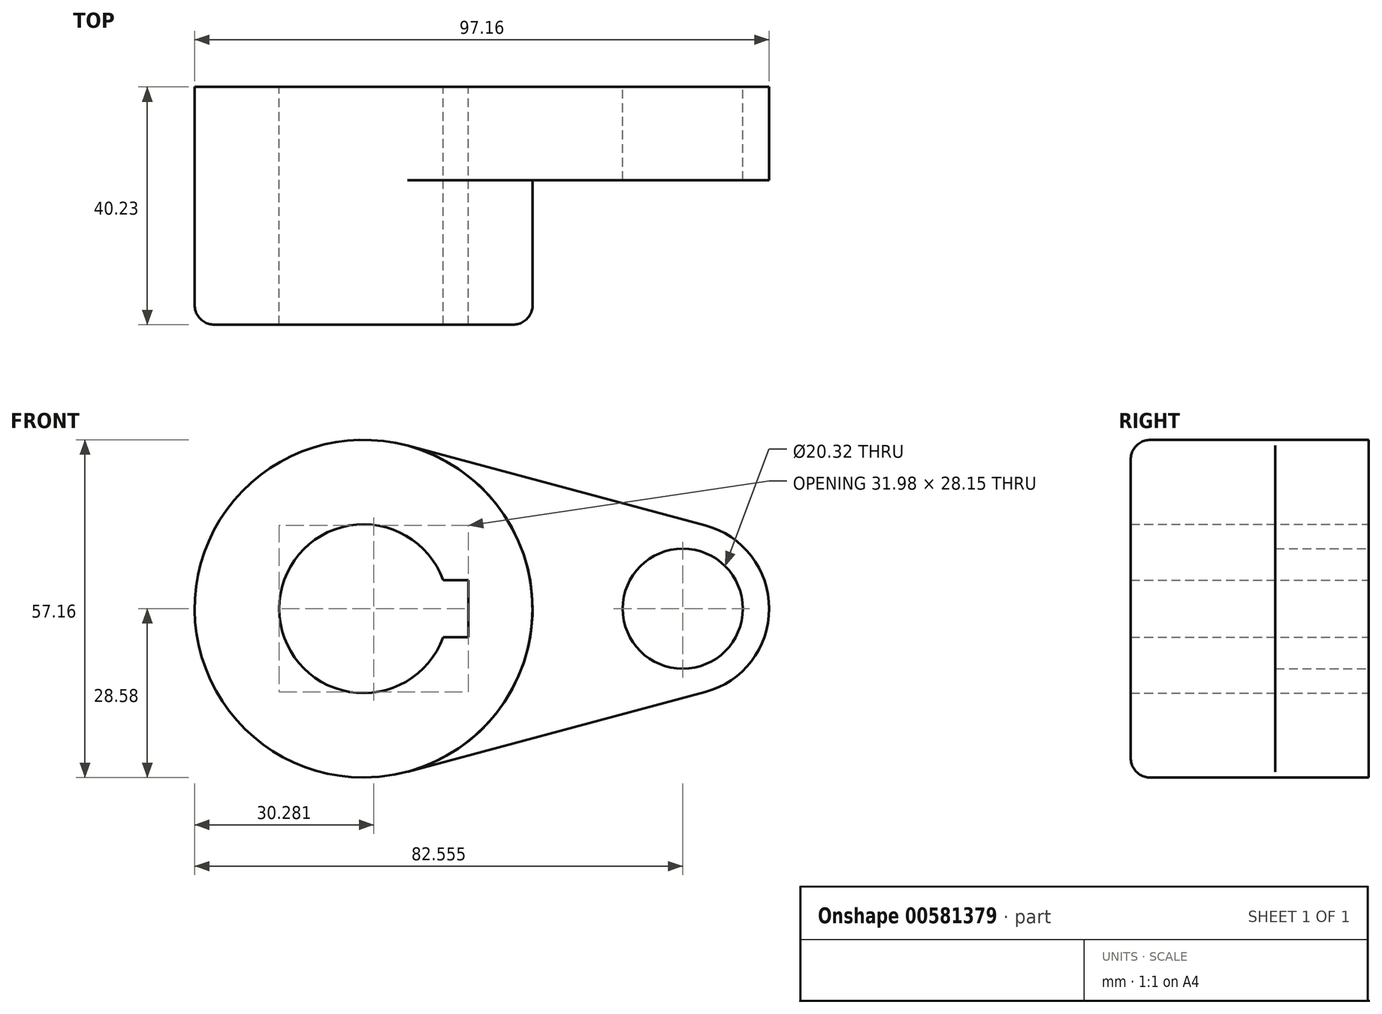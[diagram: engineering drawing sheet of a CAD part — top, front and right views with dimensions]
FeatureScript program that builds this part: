
annotation { "Feature Type Name" : "Feature", "Feature Type Description" : "" }
export const myFeature = defineFeature(function(context is Context, id is Id, definition is map)
    precondition{}
    {
        {
            var Q0;
            Q0=qCreatedBy(makeId("Front.planeOp"),FACE);
            var sketch = newSketch(context, id + "F0", { "sketchPlane" : qUnion([Q0])});
            skCircle(sketch, "E0", {"center": v(0, 0) * mm, "radius": 28.58 * mm});
            skCircle(sketch, "E1", {"center": v(0, 0) * mm, "radius": 14.29 * mm});
            skLineSegment(sketch, "E2", {"start": v(0, 0) * mm, "end": v(53.98, 0) * mm, "construction": true});
            skCircle(sketch, "E3", {"center": v(53.98, 0) * mm, "radius": 10.16 * mm});
            skCircle(sketch, "E4", {"center": v(53.98, 0) * mm, "radius": 14.6 * mm});
            skLineSegment(sketch, "E5", {"start": v(7.4, 27.6) * mm, "end": v(57.76, 14.1) * mm});
            skLineSegment(sketch, "E6", {"start": v(7.4, -27.6) * mm, "end": v(57.76, -14.1) * mm});
            skLineSegment(sketch, "E7", {"start": v(13.45, 4.83) * mm, "end": v(17.69, 4.83) * mm});
            skLineSegment(sketch, "E8", {"start": v(17.69, 4.83) * mm, "end": v(17.69, -4.83) * mm});
            skLineSegment(sketch, "E9", {"start": v(17.69, -4.83) * mm, "end": v(13.45, -4.83) * mm});
            skSolve(sketch);
        }
        {
            var Q0;
            {var subQ0=sQuery(id+"F0.wireOp",EDGE,"E7");Q0=makeQuery(id+"F0.imprint","IMPRINT",FACE,{"disambiguationData":[TD([[makeQuery(id+"F0.imprint","IMPRINT",EDGE,{"derivedFrom":subQ0}),1.0]])]});}
            extrude(context, id + "F1", {"entities" : qUnion([Q0]), "depth" : 40.23 * mm, "offsetDistance" : 25.4 * mm});
        }
        {
            var Q0;
            {var subQ0=sQuery(id+"F0.wireOp",EDGE,"E5");Q0=makeQuery(id+"F0.imprint","IMPRINT",FACE,{"disambiguationData":[TD([[makeQuery(id+"F0.imprint","IMPRINT",EDGE,{"derivedFrom":subQ0}),-1.0]])]});}
            var Q1;
            Q1=makeQuery(id+"F0.imprint","IMPRINT",FACE,{"disambiguationData":[TD([[makeQuery(id+"F0.imprint","IMPRINT",EDGE,{"derivedFrom":sQuery(id+"F0.wireOp",EDGE,"E3")}),-1.0]])]});
            extrude(context, id + "F2", {"entities" : qUnion([Q0, Q1]), "operationType" : NewBodyOperationType.ADD, "depth" : 15.77 * mm, "offsetDistance" : 25.4 * mm});
        }
        {
            var Q0;
            Q0=makeQuery(id+"F1.opExtrude","CAP_EDGE",EDGE,{"disambiguationData":[OSD([sQuery(id+"F0.wireOp",EDGE,"E0")])],"isStart":false});
            fillet(context, id + "F3", {"entities" : qUnion([Q0]), "radius" : 3.3 * mm, "tangentPropagation" : true, "allowEdgeOverflow" : false});
        }
    });
